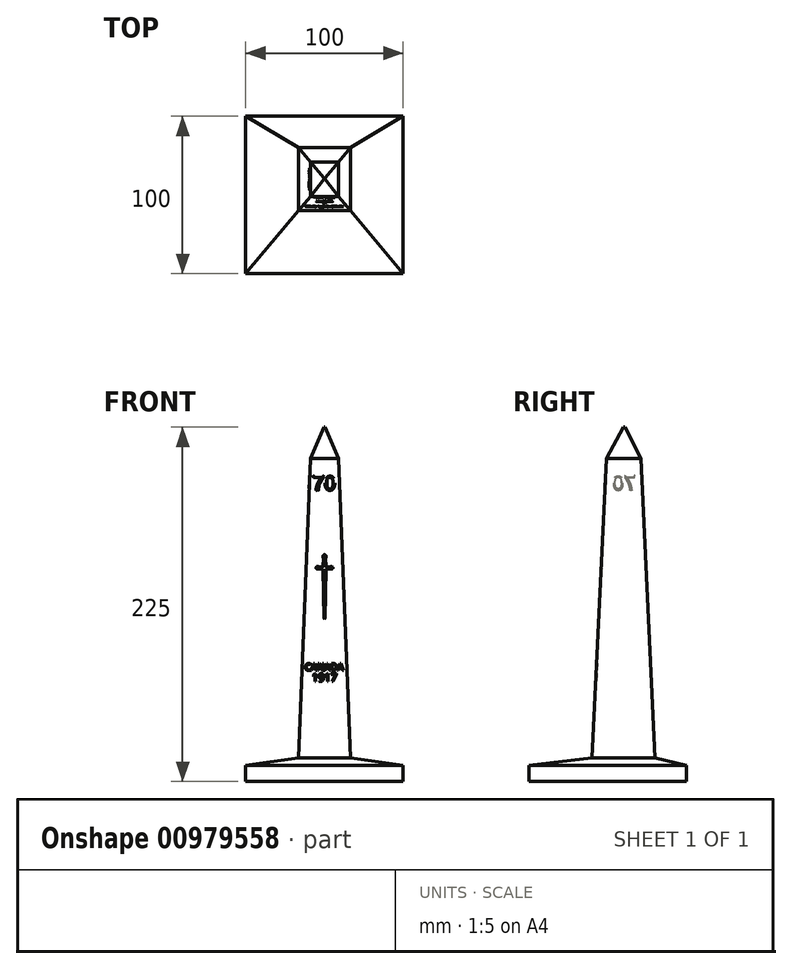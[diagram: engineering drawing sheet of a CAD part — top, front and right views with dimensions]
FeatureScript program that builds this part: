
annotation { "Feature Type Name" : "Feature", "Feature Type Description" : "" }
export const myFeature = defineFeature(function(context is Context, id is Id, definition is map)
    precondition{}
    {
        {
            var Q0;
            Q0=qCreatedBy(makeId("Top.planeOp"),FACE);
            cPlane(context, id + "F0", {"entities" : qUnion([Q0]), "cplaneType" : CPlaneType.OFFSET, "offset" : 15 * mm, "width" : 150 * mm, "height" : 150 * mm});
        }
        {
            var Q0;
            Q0=qCreatedBy(makeId("Top.planeOp"),FACE);
            cPlane(context, id + "F1", {"entities" : qUnion([Q0]), "cplaneType" : CPlaneType.OFFSET, "offset" : 205 * mm, "width" : 150 * mm, "height" : 150 * mm});
        }
        {
            var Q0;
            Q0=qCreatedBy(makeId("Top.planeOp"),FACE);
            cPlane(context, id + "F2", {"entities" : qUnion([Q0]), "cplaneType" : CPlaneType.OFFSET, "offset" : 225 * mm, "width" : 150 * mm, "height" : 150 * mm});
        }
        {
            var Q0;
            Q0=qCreatedBy(makeId("Top.planeOp"),FACE);
            var sketch = newSketch(context, id + "F3", { "sketchPlane" : qUnion([Q0])});
            skLineSegment(sketch, "E0.bottom", {"start": v(-50, 50) * mm, "end": v(50, 50) * mm});
            skLineSegment(sketch, "E0.top", {"start": v(-50, -50) * mm, "end": v(50, -50) * mm});
            skLineSegment(sketch, "E0.left", {"start": v(-50, 50) * mm, "end": v(-50, -50) * mm});
            skLineSegment(sketch, "E0.right", {"start": v(50, 50) * mm, "end": v(50, -50) * mm});
            skPoint(sketch, "E0.middle", {"position": v(0, 0) * mm});
            skSolve(sketch);
        }
        {
            var Q0;
            Q0=makeQuery(id+"F3.imprint","IMPRINT",FACE,{"disambiguationData":[TD([[makeQuery(id+"F3.imprint","IMPRINT",EDGE,{"derivedFrom":sQuery(id+"F3.wireOp",EDGE,"E0.bottom")}),-1.0]])]});
            extrude(context, id + "F4", {"entities" : qUnion([Q0]), "depth" : 10 * mm, "offsetDistance" : 25 * mm});
        }
        {
            var Q0;
            Q0=qCreatedBy(id+"F0.planeOp",FACE);
            var sketch = newSketch(context, id + "F5", { "sketchPlane" : qUnion([Q0])});
            skLineSegment(sketch, "E1.bottom", {"start": v(-16.5, 30) * mm, "end": v(16.5, 30) * mm});
            skLineSegment(sketch, "E1.top", {"start": v(-16.5, -10) * mm, "end": v(16.5, -10) * mm});
            skLineSegment(sketch, "E1.left", {"start": v(-16.5, 30) * mm, "end": v(-16.5, -10) * mm});
            skLineSegment(sketch, "E1.right", {"start": v(16.5, 30) * mm, "end": v(16.5, -10) * mm});
            skPoint(sketch, "E1.middle", {"position": v(0, 0) * mm});
            skSolve(sketch);
        }
        {
            var Q0;
            Q0=qCreatedBy(id+"F1.planeOp",FACE);
            var sketch = newSketch(context, id + "F6", { "sketchPlane" : qUnion([Q0])});
            skLineSegment(sketch, "E2.bottom", {"start": v(-9, 21) * mm, "end": v(9, 21) * mm});
            skLineSegment(sketch, "E2.top", {"start": v(-9, -1) * mm, "end": v(9, -1) * mm});
            skLineSegment(sketch, "E2.left", {"start": v(-9, 21) * mm, "end": v(-9, -1) * mm});
            skLineSegment(sketch, "E2.right", {"start": v(9, 21) * mm, "end": v(9, -1) * mm});
            skCircle(sketch, "E3", {"center": v(0, 10) * mm, "radius": 14.21 * mm, "construction": true});
            skSolve(sketch);
        }
        {
            var Q0;
            Q0=qCreatedBy(id+"F2.planeOp",FACE);
            var sketch = newSketch(context, id + "F7", { "sketchPlane" : qUnion([Q0])});
            skLineSegment(sketch, "E4.bottom", {"start": v(-0.4, 10.8) * mm, "end": v(0.4, 10.8) * mm});
            skLineSegment(sketch, "E4.top", {"start": v(-0.4, 10) * mm, "end": v(0.4, 10) * mm});
            skLineSegment(sketch, "E4.left", {"start": v(-0.4, 10.8) * mm, "end": v(-0.4, 10) * mm});
            skLineSegment(sketch, "E4.right", {"start": v(0.4, 10.8) * mm, "end": v(0.4, 10) * mm});
            skPoint(sketch, "E4.middle", {"position": v(0, 0) * mm});
            skSolve(sketch);
        }
        {
            var Q1;
            Q1=makeQuery(id+"F4.opExtrude","CAP_FACE",FACE,{"disambiguationData":[OSD([sQuery(id+"F3.wireOp",EDGE,"E0.bottom"),sQuery(id+"F3.wireOp",EDGE,"E0.top"),sQuery(id+"F3.wireOp",EDGE,"E0.left"),sQuery(id+"F3.wireOp",EDGE,"E0.right")])],"isStart":false});
            var Q2;
            Q2=makeQuery(id+"F5.imprint","IMPRINT",FACE,{"disambiguationData":[TD([[makeQuery(id+"F5.imprint","IMPRINT",EDGE,{"derivedFrom":sQuery(id+"F5.wireOp",EDGE,"E1.bottom")}),-1.0]])]});
            loft(context, id + "F8", {"operationType" : NewBodyOperationType.ADD, "sheetProfilesArray" : [{ "sheetProfileEntities" : qUnion([Q1]) }, { "sheetProfileEntities" : qUnion([Q2]) }]});
        }
        {
            var Q1;
            Q1=makeQuery(id+"F5.imprint","IMPRINT",FACE,{"disambiguationData":[TD([[makeQuery(id+"F5.imprint","IMPRINT",EDGE,{"derivedFrom":sQuery(id+"F5.wireOp",EDGE,"E1.bottom")}),-1.0]])]});
            var Q2;
            Q2=makeQuery(id+"F6.imprint","IMPRINT",FACE,{"disambiguationData":[TD([[makeQuery(id+"F6.imprint","IMPRINT",EDGE,{"derivedFrom":sQuery(id+"F6.wireOp",EDGE,"E2.bottom")}),-1.0]])]});
            loft(context, id + "F9", {"operationType" : NewBodyOperationType.ADD, "sheetProfilesArray" : [{ "sheetProfileEntities" : qUnion([Q1]) }, { "sheetProfileEntities" : qUnion([Q2]) }]});
        }
        {
            var Q1;
            Q1=makeQuery(id+"F9.opLoft","CAP_FACE",FACE,{"disambiguationData":[OSD([makeQuery(id+"F6.imprint","IMPRINT",FACE,{"disambiguationData":[TD([[makeQuery(id+"F6.imprint","IMPRINT",EDGE,{"derivedFrom":sQuery(id+"F6.wireOp",EDGE,"E2.bottom")}),-1.0]])]})])],"isStart":true});
            var Q2;
            Q2=makeQuery(id+"F7.imprint","IMPRINT",FACE,{"disambiguationData":[TD([[makeQuery(id+"F7.imprint","IMPRINT",EDGE,{"derivedFrom":sQuery(id+"F7.wireOp",EDGE,"E4.bottom")}),-1.0]])]});
            loft(context, id + "F10", {"operationType" : NewBodyOperationType.ADD, "sheetProfilesArray" : [{ "sheetProfileEntities" : qUnion([Q1]) }, { "sheetProfileEntities" : qUnion([Q2]) }]});
        }
        {
            var Q0;
            Q0=makeQuery(id+"F9.opLoft","SWEPT_FACE",FACE,{"disambiguationData":[OSD([sQuery(id+"F5.wireOp",EDGE,"E1.top"),sQuery(id+"F5.wireOp",EDGE,"E1.left"),sQuery(id+"F5.wireOp",EDGE,"E1.right"),sQuery(id+"F6.wireOp",EDGE,"E2.top"),sQuery(id+"F6.wireOp",EDGE,"E2.left"),sQuery(id+"F6.wireOp",EDGE,"E2.right")])]});
            var sketch = newSketch(context, id + "F11", { "sketchPlane" : qUnion([Q0])});
            skText(sketch, "E5", { "text": "70", "fontName": "Arimo-Regular.ttf"});
            const initialGuessF11  = {"E5": [-0.0075, 0.18463, 1, 0, 0.00945]};
            skSetInitialGuess(sketch, initialGuessF11);
            skSolve(sketch);
        }
        {
            var Q0;
            Q0=makeQuery(id+"F9.opLoft","SWEPT_FACE",FACE,{"disambiguationData":[OSD([sQuery(id+"F5.wireOp",EDGE,"E1.bottom"),sQuery(id+"F5.wireOp",EDGE,"E1.top"),sQuery(id+"F5.wireOp",EDGE,"E1.left"),sQuery(id+"F6.wireOp",EDGE,"E2.bottom"),sQuery(id+"F6.wireOp",EDGE,"E2.top"),sQuery(id+"F6.wireOp",EDGE,"E2.left")])]});
            var sketch = newSketch(context, id + "F12", { "sketchPlane" : qUnion([Q0])});
            skText(sketch, "E6", { "text": "70", "fontName": "Arimo-Regular.ttf"});
            skLineSegment(sketch, "E7.0", {"start": v(1.95, 184.5) * mm, "end": v(1.95, 185.09) * mm});
            const initialGuessF12  = {"E6": [-0.0175, 0.1845, 1, 0, 0.00945]};
            skSetInitialGuess(sketch, initialGuessF12);
            skSolve(sketch);
        }
        {
            var Q0;
            {var subQ0=sQuery(id+"F6.wireOp",EDGE,"E2.left");var subQ1=sQuery(id+"F6.wireOp",EDGE,"E2.top");var subQ3=sQuery(id+"F5.wireOp",EDGE,"E1.left");var subQ4=sQuery(id+"F5.wireOp",EDGE,"E1.top");var subQ6=sQuery(id+"F5.wireOp",EDGE,"E1.right");var subQ11=sQuery(id+"F6.wireOp",EDGE,"E2.right");Q0=makeQuery(id+"F14.boolean.opBoolean","SPLIT",FACE,{"disambiguationData":[TD([makeQuery(id+"F14.opExtrude","SWEPT_FACE",FACE,{"disambiguationData":[OSD([sQuery(id+"F11.wireOp",EDGE,"E5.sketch_text.stroke-0")])]})])],"derivedFrom":makeQuery(id+"F9.opLoft","SWEPT_FACE",FACE,{"disambiguationData":[OSD([subQ4,subQ3,subQ6,subQ1,subQ0,subQ11])]})});}
            var sketch = newSketch(context, id + "F13", { "sketchPlane" : qUnion([Q0])});
            skLineSegment(sketch, "E8", {"start": v(0, 102.63) * mm, "end": v(-0.4, 103.13) * mm});
            skLineSegment(sketch, "E9", {"start": v(-0.4, 103.13) * mm, "end": v(-1, 134.43) * mm});
            skLineSegment(sketch, "E10", {"start": v(-1, 134.43) * mm, "end": v(-3.74, 134.68) * mm});
            skLineSegment(sketch, "E11", {"start": v(0, 102.63) * mm, "end": v(0, 143.63) * mm, "construction": true});
            skCircle(sketch, "E12", {"center": v(-4.4, 135.29) * mm, "radius": 0.9 * mm});
            skPoint(sketch, "E12.second.point", {"position": v(-3.74, 135.9) * mm});
            skPoint(sketch, "E12.third.point", {"position": v(-5.3, 135.25) * mm});
            skLineSegment(sketch, "E13", {"start": v(-3.74, 135.9) * mm, "end": v(-1, 136.03) * mm});
            skLineSegment(sketch, "E14", {"start": v(-1, 136.03) * mm, "end": v(-0.66, 141.52) * mm});
            skArc(sketch, "E15", {"start": v(0, 143.63) * mm, "mid": v(-1.03, 142.8) * mm, "end": v(-0.66, 141.52) * mm});
            skArc(sketch, "E16.MirrorCS", {"start": v(0, 143.63) * mm, "mid": v(1.03, 142.8) * mm, "end": v(0.66, 141.52) * mm});
            skLineSegment(sketch, "E17.MirrorCS", {"start": v(1, 136.03) * mm, "end": v(0.66, 141.52) * mm});
            skLineSegment(sketch, "E18.MirrorCS", {"start": v(3.74, 135.9) * mm, "end": v(1, 136.03) * mm});
            skCircle(sketch, "E19.MirrorC", {"center": v(4.4, 135.29) * mm, "radius": 0.9 * mm});
            skLineSegment(sketch, "E20.MirrorCS", {"start": v(1, 134.43) * mm, "end": v(3.74, 134.68) * mm});
            skLineSegment(sketch, "E21.MirrorCS", {"start": v(0.4, 103.13) * mm, "end": v(1, 134.43) * mm});
            skLineSegment(sketch, "E22.MirrorCS", {"start": v(0, 102.63) * mm, "end": v(0.4, 103.13) * mm});
            skSolve(sketch);
        }
        {
            var Q0;
            Q0=qSketchRegion(id+"F11",true);
            extrude(context, id + "F14", {"entities" : qUnion([Q0]), "operationType" : NewBodyOperationType.REMOVE, "oppositeDirection" : true, "depth" : .4 * mm, "offsetDistance" : 25 * mm});
        }
        {
            var Q0;
            Q0 = qSketchRegion(id + "F12", true);
            extrude(context, id + "F15", {"entities" : qUnion([Q0]), "operationType" : NewBodyOperationType.REMOVE, "oppositeDirection" : true, "depth" : .4 * mm, "offsetDistance" : 25 * mm});
        }
        {
            var Q0;
            Q0=qSketchRegion(id+"F13",true);
            extrude(context, id + "F16", {"entities" : qUnion([Q0]), "operationType" : NewBodyOperationType.REMOVE, "oppositeDirection" : true, "depth" : .4 * mm, "offsetDistance" : 25 * mm});
        }
        {
            var Q0;
            Q0=makeQuery(id+"F14.boolean.opBoolean","COPY",EDGE,{"derivedFrom":makeQuery(id+"F14.opExtrude","CAP_EDGE",EDGE,{"disambiguationData":[OSD([sQuery(id+"F11.wireOp",EDGE,"E5.sketch_text.stroke-5")])],"isStart":true})});
            var Q1;
            Q1=makeQuery(id+"F14.boolean.opBoolean","COPY",EDGE,{"derivedFrom":makeQuery(id+"F14.opExtrude","CAP_EDGE",EDGE,{"disambiguationData":[OSD([sQuery(id+"F11.wireOp",EDGE,"E5.sketch_text.stroke-6")])],"isStart":true})});
            var Q2;
            Q2=makeQuery(id+"F14.boolean.opBoolean","COPY",EDGE,{"derivedFrom":makeQuery(id+"F14.opExtrude","CAP_EDGE",EDGE,{"disambiguationData":[OSD([sQuery(id+"F11.wireOp",EDGE,"E5.sketch_text.stroke-7")])],"isStart":true})});
            var Q3;
            Q3=makeQuery(id+"F14.boolean.opBoolean","COPY",EDGE,{"derivedFrom":makeQuery(id+"F14.opExtrude","CAP_EDGE",EDGE,{"disambiguationData":[OSD([sQuery(id+"F11.wireOp",EDGE,"E5.sketch_text.stroke-8")])],"isStart":true})});
            var Q4;
            Q4=makeQuery(id+"F14.boolean.opBoolean","COPY",EDGE,{"derivedFrom":makeQuery(id+"F14.opExtrude","CAP_EDGE",EDGE,{"disambiguationData":[OSD([sQuery(id+"F11.wireOp",EDGE,"E5.sketch_text.stroke-0")])],"isStart":true})});
            var Q5;
            Q5=makeQuery(id+"F14.boolean.opBoolean","COPY",EDGE,{"derivedFrom":makeQuery(id+"F14.opExtrude","CAP_EDGE",EDGE,{"disambiguationData":[OSD([sQuery(id+"F11.wireOp",EDGE,"E5.sketch_text.stroke-9")])],"isStart":true})});
            var Q6;
            Q6=makeQuery(id+"F14.boolean.opBoolean","COPY",EDGE,{"derivedFrom":makeQuery(id+"F14.opExtrude","CAP_EDGE",EDGE,{"disambiguationData":[OSD([sQuery(id+"F11.wireOp",EDGE,"E5.sketch_text.stroke-1")])],"isStart":true})});
            var Q7;
            Q7=makeQuery(id+"F14.boolean.opBoolean","COPY",EDGE,{"derivedFrom":makeQuery(id+"F14.opExtrude","CAP_EDGE",EDGE,{"disambiguationData":[OSD([sQuery(id+"F11.wireOp",EDGE,"E5.sketch_text.stroke-2")])],"isStart":true})});
            var Q8;
            Q8=makeQuery(id+"F14.boolean.opBoolean","COPY",EDGE,{"derivedFrom":makeQuery(id+"F14.opExtrude","CAP_EDGE",EDGE,{"disambiguationData":[OSD([sQuery(id+"F11.wireOp",EDGE,"E5.sketch_text.stroke-3")])],"isStart":true})});
            var Q9;
            Q9=makeQuery(id+"F14.boolean.opBoolean","COPY",EDGE,{"derivedFrom":makeQuery(id+"F14.opExtrude","CAP_EDGE",EDGE,{"disambiguationData":[OSD([sQuery(id+"F11.wireOp",EDGE,"E5.sketch_text.stroke-4")])],"isStart":true})});
            var Q10;
            Q10=makeQuery(id+"F14.boolean.opBoolean","COPY",EDGE,{"derivedFrom":makeQuery(id+"F14.opExtrude","CAP_EDGE",EDGE,{"disambiguationData":[OSD([sQuery(id+"F11.wireOp",EDGE,"E5.sketch_text.stroke-6")])],"isStart":false})});
            var Q11;
            Q11=makeQuery(id+"F14.boolean.opBoolean","COPY",EDGE,{"derivedFrom":makeQuery(id+"F14.opExtrude","CAP_EDGE",EDGE,{"disambiguationData":[OSD([sQuery(id+"F11.wireOp",EDGE,"E5.sketch_text.stroke-7")])],"isStart":false})});
            var Q12;
            Q12=makeQuery(id+"F14.boolean.opBoolean","COPY",EDGE,{"derivedFrom":makeQuery(id+"F14.opExtrude","CAP_EDGE",EDGE,{"disambiguationData":[OSD([sQuery(id+"F11.wireOp",EDGE,"E5.sketch_text.stroke-8")])],"isStart":false})});
            var Q13;
            Q13=makeQuery(id+"F14.boolean.opBoolean","COPY",EDGE,{"derivedFrom":makeQuery(id+"F14.opExtrude","CAP_EDGE",EDGE,{"disambiguationData":[OSD([sQuery(id+"F11.wireOp",EDGE,"E5.sketch_text.stroke-9")])],"isStart":false})});
            var Q14;
            Q14=makeQuery(id+"F14.boolean.opBoolean","COPY",EDGE,{"derivedFrom":makeQuery(id+"F14.opExtrude","CAP_EDGE",EDGE,{"disambiguationData":[OSD([sQuery(id+"F11.wireOp",EDGE,"E5.sketch_text.stroke-0")])],"isStart":false})});
            var Q15;
            Q15=makeQuery(id+"F14.boolean.opBoolean","COPY",EDGE,{"derivedFrom":makeQuery(id+"F14.opExtrude","CAP_EDGE",EDGE,{"disambiguationData":[OSD([sQuery(id+"F11.wireOp",EDGE,"E5.sketch_text.stroke-3")])],"isStart":false})});
            var Q16;
            Q16=makeQuery(id+"F14.boolean.opBoolean","COPY",EDGE,{"derivedFrom":makeQuery(id+"F14.opExtrude","CAP_EDGE",EDGE,{"disambiguationData":[OSD([sQuery(id+"F11.wireOp",EDGE,"E5.sketch_text.stroke-4")])],"isStart":false})});
            var Q17;
            Q17=makeQuery(id+"F14.boolean.opBoolean","COPY",EDGE,{"derivedFrom":makeQuery(id+"F14.opExtrude","CAP_EDGE",EDGE,{"disambiguationData":[OSD([sQuery(id+"F11.wireOp",EDGE,"E5.sketch_text.stroke-5")])],"isStart":false})});
            var Q18;
            Q18=makeQuery(id+"F14.boolean.opBoolean","COPY",EDGE,{"derivedFrom":makeQuery(id+"F14.opExtrude","CAP_EDGE",EDGE,{"disambiguationData":[OSD([sQuery(id+"F11.wireOp",EDGE,"E5.sketch_text.stroke-1")])],"isStart":false})});
            var Q19;
            Q19=makeQuery(id+"F14.boolean.opBoolean","COPY",EDGE,{"derivedFrom":makeQuery(id+"F14.opExtrude","CAP_EDGE",EDGE,{"disambiguationData":[OSD([sQuery(id+"F11.wireOp",EDGE,"E5.sketch_text.stroke-2")])],"isStart":false})});
            var Q20;
            Q20=makeQuery(id+"F14.boolean.opBoolean","COPY",EDGE,{"derivedFrom":makeQuery(id+"F14.opExtrude","CAP_EDGE",EDGE,{"disambiguationData":[OSD([sQuery(id+"F11.wireOp",EDGE,"E5.sketch_text.stroke-10")])],"isStart":false})});
            var Q21;
            Q21=makeQuery(id+"F14.boolean.opBoolean","COPY",EDGE,{"derivedFrom":makeQuery(id+"F14.opExtrude","CAP_EDGE",EDGE,{"disambiguationData":[OSD([sQuery(id+"F11.wireOp",EDGE,"E5.sketch_text.stroke-10")])],"isStart":true})});
            var Q22;
            Q22=makeQuery(id+"F14.boolean.opBoolean","COPY",EDGE,{"derivedFrom":makeQuery(id+"F14.opExtrude","CAP_EDGE",EDGE,{"disambiguationData":[OSD([sQuery(id+"F11.wireOp",EDGE,"E5.sketch_text.stroke-22")])],"isStart":false})});
            var Q23;
            Q23=makeQuery(id+"F14.boolean.opBoolean","COPY",EDGE,{"derivedFrom":makeQuery(id+"F14.opExtrude","CAP_EDGE",EDGE,{"disambiguationData":[OSD([sQuery(id+"F11.wireOp",EDGE,"E5.sketch_text.stroke-21")])],"isStart":true})});
            var Q24;
            Q24=makeQuery(id+"F14.boolean.opBoolean","COPY",EDGE,{"derivedFrom":makeQuery(id+"F14.opExtrude","CAP_EDGE",EDGE,{"disambiguationData":[OSD([sQuery(id+"F13.wireOp",EDGE,"E15")])],"isStart":false})});
            var Q25;
            Q25=makeQuery(id+"F14.boolean.opBoolean","COPY",EDGE,{"derivedFrom":makeQuery(id+"F14.opExtrude","CAP_EDGE",EDGE,{"disambiguationData":[OSD([sQuery(id+"F13.wireOp",EDGE,"E16.MirrorCS")])],"isStart":false})});
            var Q26;
            Q26=makeQuery(id+"F14.boolean.opBoolean","COPY",EDGE,{"derivedFrom":makeQuery(id+"F14.opExtrude","CAP_EDGE",EDGE,{"disambiguationData":[OSD([sQuery(id+"F13.wireOp",EDGE,"E16.MirrorCS")])],"isStart":true})});
            var Q27;
            Q27=makeQuery(id+"F14.boolean.opBoolean","COPY",EDGE,{"derivedFrom":makeQuery(id+"F14.opExtrude","CAP_EDGE",EDGE,{"disambiguationData":[OSD([sQuery(id+"F13.wireOp",EDGE,"E15")])],"isStart":true})});
            var Q28;
            Q28=makeQuery(id+"F14.boolean.opBoolean","COPY",EDGE,{"derivedFrom":makeQuery(id+"F14.opExtrude","CAP_EDGE",EDGE,{"disambiguationData":[OSD([sQuery(id+"F13.wireOp",EDGE,"E17.MirrorCS")])],"isStart":false})});
            var Q29;
            Q29=makeQuery(id+"F14.boolean.opBoolean","COPY",EDGE,{"derivedFrom":makeQuery(id+"F14.opExtrude","CAP_EDGE",EDGE,{"disambiguationData":[OSD([sQuery(id+"F13.wireOp",EDGE,"E17.MirrorCS")])],"isStart":true})});
            var Q30;
            Q30=makeQuery(id+"F14.boolean.opBoolean","COPY",EDGE,{"derivedFrom":makeQuery(id+"F14.opExtrude","CAP_EDGE",EDGE,{"disambiguationData":[OSD([sQuery(id+"F13.wireOp",EDGE,"E14")])],"isStart":false})});
            var Q31;
            Q31=makeQuery(id+"F14.boolean.opBoolean","COPY",EDGE,{"derivedFrom":makeQuery(id+"F14.opExtrude","CAP_EDGE",EDGE,{"disambiguationData":[OSD([sQuery(id+"F13.wireOp",EDGE,"E14")])],"isStart":true})});
            var Q32;
            Q32=makeQuery(id+"F14.boolean.opBoolean","COPY",EDGE,{"derivedFrom":makeQuery(id+"F14.opExtrude","CAP_EDGE",EDGE,{"disambiguationData":[OSD([sQuery(id+"F13.wireOp",EDGE,"E13")])],"isStart":false})});
            var Q33;
            Q33=makeQuery(id+"F14.boolean.opBoolean","COPY",EDGE,{"derivedFrom":makeQuery(id+"F14.opExtrude","CAP_EDGE",EDGE,{"disambiguationData":[OSD([sQuery(id+"F13.wireOp",EDGE,"E13")])],"isStart":true})});
            var Q34;
            Q34=makeQuery(id+"F14.boolean.opBoolean","COPY",EDGE,{"derivedFrom":makeQuery(id+"F14.opExtrude","CAP_EDGE",EDGE,{"disambiguationData":[OSD([sQuery(id+"F13.wireOp",EDGE,"E12")])],"isStart":false})});
            var Q35;
            Q35=makeQuery(id+"F14.boolean.opBoolean","COPY",EDGE,{"derivedFrom":makeQuery(id+"F14.opExtrude","CAP_EDGE",EDGE,{"disambiguationData":[OSD([sQuery(id+"F13.wireOp",EDGE,"E12")])],"isStart":true})});
            var Q36;
            Q36=makeQuery(id+"F14.boolean.opBoolean","COPY",EDGE,{"derivedFrom":makeQuery(id+"F14.opExtrude","CAP_EDGE",EDGE,{"disambiguationData":[OSD([sQuery(id+"F13.wireOp",EDGE,"E18.MirrorCS")])],"isStart":false})});
            var Q37;
            Q37=makeQuery(id+"F14.boolean.opBoolean","COPY",EDGE,{"derivedFrom":makeQuery(id+"F14.opExtrude","CAP_EDGE",EDGE,{"disambiguationData":[OSD([sQuery(id+"F13.wireOp",EDGE,"E18.MirrorCS")])],"isStart":true})});
            var Q38;
            Q38=makeQuery(id+"F14.boolean.opBoolean","COPY",EDGE,{"derivedFrom":makeQuery(id+"F14.opExtrude","CAP_EDGE",EDGE,{"disambiguationData":[OSD([sQuery(id+"F13.wireOp",EDGE,"E19.MirrorC")])],"isStart":false})});
            var Q39;
            Q39=makeQuery(id+"F14.boolean.opBoolean","COPY",EDGE,{"derivedFrom":makeQuery(id+"F14.opExtrude","CAP_EDGE",EDGE,{"disambiguationData":[OSD([sQuery(id+"F13.wireOp",EDGE,"E19.MirrorC")])],"isStart":true})});
            var Q40;
            Q40=makeQuery(id+"F14.boolean.opBoolean","COPY",EDGE,{"derivedFrom":makeQuery(id+"F14.opExtrude","CAP_EDGE",EDGE,{"disambiguationData":[OSD([sQuery(id+"F13.wireOp",EDGE,"E20.MirrorCS")])],"isStart":false})});
            var Q41;
            Q41=makeQuery(id+"F14.boolean.opBoolean","COPY",EDGE,{"derivedFrom":makeQuery(id+"F14.opExtrude","CAP_EDGE",EDGE,{"disambiguationData":[OSD([sQuery(id+"F13.wireOp",EDGE,"E20.MirrorCS")])],"isStart":true})});
            var Q42;
            Q42=makeQuery(id+"F14.boolean.opBoolean","COPY",EDGE,{"derivedFrom":makeQuery(id+"F14.opExtrude","CAP_EDGE",EDGE,{"disambiguationData":[OSD([sQuery(id+"F13.wireOp",EDGE,"E10")])],"isStart":false})});
            var Q43;
            Q43=makeQuery(id+"F14.boolean.opBoolean","COPY",EDGE,{"derivedFrom":makeQuery(id+"F14.opExtrude","CAP_EDGE",EDGE,{"disambiguationData":[OSD([sQuery(id+"F13.wireOp",EDGE,"E21.MirrorCS")])],"isStart":false})});
            var Q44;
            Q44=makeQuery(id+"F14.boolean.opBoolean","COPY",EDGE,{"derivedFrom":makeQuery(id+"F14.opExtrude","CAP_EDGE",EDGE,{"disambiguationData":[OSD([sQuery(id+"F13.wireOp",EDGE,"E21.MirrorCS")])],"isStart":true})});
            var Q45;
            Q45=makeQuery(id+"F14.boolean.opBoolean","COPY",EDGE,{"derivedFrom":makeQuery(id+"F14.opExtrude","CAP_EDGE",EDGE,{"disambiguationData":[OSD([sQuery(id+"F13.wireOp",EDGE,"E10")])],"isStart":true})});
            var Q46;
            Q46=makeQuery(id+"F14.boolean.opBoolean","COPY",EDGE,{"derivedFrom":makeQuery(id+"F14.opExtrude","CAP_EDGE",EDGE,{"disambiguationData":[OSD([sQuery(id+"F13.wireOp",EDGE,"E9")])],"isStart":false})});
            var Q47;
            Q47=makeQuery(id+"F14.boolean.opBoolean","COPY",EDGE,{"derivedFrom":makeQuery(id+"F14.opExtrude","CAP_EDGE",EDGE,{"disambiguationData":[OSD([sQuery(id+"F13.wireOp",EDGE,"E9")])],"isStart":true})});
            var Q48;
            Q48=makeQuery(id+"F14.boolean.opBoolean","COPY",EDGE,{"derivedFrom":makeQuery(id+"F14.opExtrude","CAP_EDGE",EDGE,{"disambiguationData":[OSD([sQuery(id+"F13.wireOp",EDGE,"E22.MirrorCS")])],"isStart":false})});
            var Q49;
            Q49=makeQuery(id+"F14.boolean.opBoolean","COPY",EDGE,{"derivedFrom":makeQuery(id+"F14.opExtrude","CAP_EDGE",EDGE,{"disambiguationData":[OSD([sQuery(id+"F13.wireOp",EDGE,"E22.MirrorCS")])],"isStart":true})});
            var Q50;
            Q50=makeQuery(id+"F14.boolean.opBoolean","COPY",EDGE,{"derivedFrom":makeQuery(id+"F14.opExtrude","CAP_EDGE",EDGE,{"disambiguationData":[OSD([sQuery(id+"F13.wireOp",EDGE,"E8")])],"isStart":true})});
            var Q51;
            Q51=makeQuery(id+"F14.boolean.opBoolean","COPY",EDGE,{"derivedFrom":makeQuery(id+"F14.opExtrude","CAP_EDGE",EDGE,{"disambiguationData":[OSD([sQuery(id+"F13.wireOp",EDGE,"E8")])],"isStart":false})});
            var Q52;
            Q52=makeQuery(id+"F15.boolean.opBoolean","COPY",EDGE,{"derivedFrom":makeQuery(id+"F15.opExtrude","CAP_EDGE",EDGE,{"disambiguationData":[OSD([sQuery(id+"F12.wireOp",EDGE,"E6.sketch_text.stroke-8")])],"isStart":true})});
            var Q53;
            Q53=makeQuery(id+"F15.boolean.opBoolean","COPY",EDGE,{"derivedFrom":makeQuery(id+"F15.opExtrude","CAP_EDGE",EDGE,{"disambiguationData":[OSD([sQuery(id+"F12.wireOp",EDGE,"E6.sketch_text.stroke-14")])],"isStart":false})});
            var Q54;
            Q54=makeQuery(id+"F15.boolean.opBoolean","COPY",EDGE,{"derivedFrom":makeQuery(id+"F15.opExtrude","CAP_EDGE",EDGE,{"disambiguationData":[OSD([sQuery(id+"F12.wireOp",EDGE,"E6.sketch_text.stroke-20")])],"isStart":true})});
            var Q55;
            Q55=makeQuery(id+"F15.boolean.opBoolean","COPY",EDGE,{"derivedFrom":makeQuery(id+"F15.opExtrude","CAP_EDGE",EDGE,{"disambiguationData":[OSD([sQuery(id+"F12.wireOp",EDGE,"E6.sketch_text.stroke-5")])],"isStart":true})});
            var Q56;
            Q56=makeQuery(id+"F15.boolean.opBoolean","COPY",EDGE,{"derivedFrom":makeQuery(id+"F15.opExtrude","CAP_EDGE",EDGE,{"disambiguationData":[OSD([sQuery(id+"F12.wireOp",EDGE,"E6.sketch_text.stroke-6")])],"isStart":true})});
            var Q57;
            Q57=makeQuery(id+"F15.boolean.opBoolean","COPY",EDGE,{"derivedFrom":makeQuery(id+"F15.opExtrude","CAP_EDGE",EDGE,{"disambiguationData":[OSD([sQuery(id+"F12.wireOp",EDGE,"E6.sketch_text.stroke-7")])],"isStart":true})});
            var Q58;
            Q58=makeQuery(id+"F15.boolean.opBoolean","COPY",EDGE,{"derivedFrom":makeQuery(id+"F15.opExtrude","CAP_EDGE",EDGE,{"disambiguationData":[OSD([sQuery(id+"F12.wireOp",EDGE,"E6.sketch_text.stroke-0")])],"isStart":true})});
            var Q59;
            Q59=makeQuery(id+"F15.boolean.opBoolean","COPY",EDGE,{"derivedFrom":makeQuery(id+"F15.opExtrude","CAP_EDGE",EDGE,{"disambiguationData":[OSD([sQuery(id+"F12.wireOp",EDGE,"E6.sketch_text.stroke-9")])],"isStart":true})});
            var Q60;
            Q60=makeQuery(id+"F15.boolean.opBoolean","COPY",EDGE,{"derivedFrom":makeQuery(id+"F15.opExtrude","CAP_EDGE",EDGE,{"disambiguationData":[OSD([sQuery(id+"F12.wireOp",EDGE,"E6.sketch_text.stroke-3")])],"isStart":false})});
            var Q61;
            Q61=makeQuery(id+"F15.boolean.opBoolean","COPY",EDGE,{"derivedFrom":makeQuery(id+"F15.opExtrude","CAP_EDGE",EDGE,{"disambiguationData":[OSD([sQuery(id+"F12.wireOp",EDGE,"E6.sketch_text.stroke-14")])],"isStart":true})});
            var Q62;
            Q62=makeQuery(id+"F15.boolean.opBoolean","COPY",EDGE,{"derivedFrom":makeQuery(id+"F15.opExtrude","CAP_EDGE",EDGE,{"disambiguationData":[OSD([sQuery(id+"F12.wireOp",EDGE,"E6.sketch_text.stroke-21")])],"isStart":false})});
            var Q63;
            Q63=makeQuery(id+"F15.boolean.opBoolean","COPY",EDGE,{"derivedFrom":makeQuery(id+"F15.opExtrude","CAP_EDGE",EDGE,{"disambiguationData":[OSD([sQuery(id+"F12.wireOp",EDGE,"E6.sketch_text.stroke-8")])],"isStart":false})});
            var Q64;
            Q64=makeQuery(id+"F15.boolean.opBoolean","COPY",EDGE,{"derivedFrom":makeQuery(id+"F15.opExtrude","CAP_EDGE",EDGE,{"disambiguationData":[OSD([sQuery(id+"F12.wireOp",EDGE,"E6.sketch_text.stroke-7")])],"isStart":false})});
            var Q65;
            Q65=makeQuery(id+"F15.boolean.opBoolean","COPY",EDGE,{"derivedFrom":makeQuery(id+"F15.opExtrude","CAP_EDGE",EDGE,{"disambiguationData":[OSD([sQuery(id+"F12.wireOp",EDGE,"E6.sketch_text.stroke-6")])],"isStart":false})});
            var Q66;
            Q66=makeQuery(id+"F15.boolean.opBoolean","COPY",EDGE,{"derivedFrom":makeQuery(id+"F15.opExtrude","CAP_EDGE",EDGE,{"disambiguationData":[OSD([sQuery(id+"F12.wireOp",EDGE,"E6.sketch_text.stroke-9")])],"isStart":false})});
            var Q67;
            Q67=makeQuery(id+"F15.boolean.opBoolean","COPY",EDGE,{"derivedFrom":makeQuery(id+"F15.opExtrude","CAP_EDGE",EDGE,{"disambiguationData":[OSD([sQuery(id+"F12.wireOp",EDGE,"E6.sketch_text.stroke-0")])],"isStart":false})});
            var Q68;
            Q68=makeQuery(id+"F15.boolean.opBoolean","COPY",EDGE,{"derivedFrom":makeQuery(id+"F15.opExtrude","CAP_EDGE",EDGE,{"disambiguationData":[OSD([sQuery(id+"F12.wireOp",EDGE,"E6.sketch_text.stroke-5")])],"isStart":false})});
            var Q69;
            Q69=makeQuery(id+"F15.boolean.opBoolean","COPY",EDGE,{"derivedFrom":makeQuery(id+"F15.opExtrude","CAP_EDGE",EDGE,{"disambiguationData":[OSD([sQuery(id+"F12.wireOp",EDGE,"E6.sketch_text.stroke-3")])],"isStart":true})});
            fillet(context, id + "F17", {"entities" : qUnion([Q0, Q1, Q2, Q3, Q4, Q5, Q6, Q7, Q8, Q9, Q10, Q11, Q12, Q13, Q14, Q15, Q16, Q17, Q18, Q19, Q20, Q21, Q22, Q23, Q24, Q25, Q26, Q27, Q28, Q29, Q30, Q31, Q32, Q33, Q34, Q35, Q36, Q37, Q38, Q39, Q40, Q41, Q42, Q43, Q44, Q45, Q46, Q47, Q48, Q49, Q50, Q51, Q52, Q53, Q54, Q55, Q56, Q57, Q58, Q59, Q60, Q61, Q62, Q63, Q64, Q65, Q66, Q67, Q68, Q69]), "radius" : .2 * mm, "tangentPropagation" : true, "allowEdgeOverflow" : false});
        }
        {
            var Q0;
            Q0=makeQuery(id+"F16.boolean.opBoolean","COPY",EDGE,{"derivedFrom":makeQuery(id+"F16.opExtrude","CAP_EDGE",EDGE,{"disambiguationData":[OSD([sQuery(id+"F13.wireOp",EDGE,"E16.MirrorCS")])],"isStart":false})});
            var Q1;
            Q1=makeQuery(id+"F16.boolean.opBoolean","COPY",EDGE,{"derivedFrom":makeQuery(id+"F16.opExtrude","CAP_EDGE",EDGE,{"disambiguationData":[OSD([sQuery(id+"F13.wireOp",EDGE,"E16.MirrorCS")])],"isStart":true})});
            var Q2;
            Q2=makeQuery(id+"F16.boolean.opBoolean","COPY",EDGE,{"derivedFrom":makeQuery(id+"F16.opExtrude","CAP_EDGE",EDGE,{"disambiguationData":[OSD([sQuery(id+"F13.wireOp",EDGE,"E15")])],"isStart":true})});
            var Q3;
            Q3=makeQuery(id+"F16.boolean.opBoolean","COPY",EDGE,{"derivedFrom":makeQuery(id+"F16.opExtrude","CAP_EDGE",EDGE,{"disambiguationData":[OSD([sQuery(id+"F13.wireOp",EDGE,"E15")])],"isStart":false})});
            var Q4;
            Q4=makeQuery(id+"F16.boolean.opBoolean","COPY",EDGE,{"derivedFrom":makeQuery(id+"F16.opExtrude","CAP_EDGE",EDGE,{"disambiguationData":[OSD([sQuery(id+"F13.wireOp",EDGE,"E14")])],"isStart":false})});
            var Q5;
            Q5=makeQuery(id+"F16.boolean.opBoolean","COPY",EDGE,{"derivedFrom":makeQuery(id+"F16.opExtrude","CAP_EDGE",EDGE,{"disambiguationData":[OSD([sQuery(id+"F13.wireOp",EDGE,"E14")])],"isStart":true})});
            var Q6;
            Q6=makeQuery(id+"F16.boolean.opBoolean","COPY",EDGE,{"derivedFrom":makeQuery(id+"F16.opExtrude","CAP_EDGE",EDGE,{"disambiguationData":[OSD([sQuery(id+"F13.wireOp",EDGE,"E17.MirrorCS")])],"isStart":false})});
            var Q7;
            Q7=makeQuery(id+"F16.boolean.opBoolean","COPY",EDGE,{"derivedFrom":makeQuery(id+"F16.opExtrude","CAP_EDGE",EDGE,{"disambiguationData":[OSD([sQuery(id+"F13.wireOp",EDGE,"E17.MirrorCS")])],"isStart":true})});
            var Q8;
            Q8=makeQuery(id+"F16.boolean.opBoolean","COPY",EDGE,{"derivedFrom":makeQuery(id+"F16.opExtrude","CAP_EDGE",EDGE,{"disambiguationData":[OSD([sQuery(id+"F13.wireOp",EDGE,"E18.MirrorCS")])],"isStart":false})});
            var Q9;
            Q9=makeQuery(id+"F16.boolean.opBoolean","COPY",EDGE,{"derivedFrom":makeQuery(id+"F16.opExtrude","CAP_EDGE",EDGE,{"disambiguationData":[OSD([sQuery(id+"F13.wireOp",EDGE,"E18.MirrorCS")])],"isStart":true})});
            var Q10;
            Q10=makeQuery(id+"F16.boolean.opBoolean","COPY",EDGE,{"derivedFrom":makeQuery(id+"F16.opExtrude","CAP_EDGE",EDGE,{"disambiguationData":[OSD([sQuery(id+"F13.wireOp",EDGE,"E19.MirrorC")])],"isStart":false})});
            var Q11;
            Q11=makeQuery(id+"F16.boolean.opBoolean","COPY",EDGE,{"derivedFrom":makeQuery(id+"F16.opExtrude","CAP_EDGE",EDGE,{"disambiguationData":[OSD([sQuery(id+"F13.wireOp",EDGE,"E19.MirrorC")])],"isStart":true})});
            var Q12;
            Q12=makeQuery(id+"F16.boolean.opBoolean","COPY",EDGE,{"derivedFrom":makeQuery(id+"F16.opExtrude","CAP_EDGE",EDGE,{"disambiguationData":[OSD([sQuery(id+"F13.wireOp",EDGE,"E20.MirrorCS")])],"isStart":true})});
            var Q13;
            Q13=makeQuery(id+"F16.boolean.opBoolean","COPY",EDGE,{"derivedFrom":makeQuery(id+"F16.opExtrude","CAP_EDGE",EDGE,{"disambiguationData":[OSD([sQuery(id+"F13.wireOp",EDGE,"E20.MirrorCS")])],"isStart":false})});
            var Q14;
            Q14=makeQuery(id+"F16.boolean.opBoolean","COPY",EDGE,{"derivedFrom":makeQuery(id+"F16.opExtrude","CAP_EDGE",EDGE,{"disambiguationData":[OSD([sQuery(id+"F13.wireOp",EDGE,"E10")])],"isStart":true})});
            var Q15;
            Q15=makeQuery(id+"F16.boolean.opBoolean","COPY",EDGE,{"derivedFrom":makeQuery(id+"F16.opExtrude","CAP_EDGE",EDGE,{"disambiguationData":[OSD([sQuery(id+"F13.wireOp",EDGE,"E10")])],"isStart":false})});
            var Q16;
            Q16=makeQuery(id+"F16.boolean.opBoolean","COPY",EDGE,{"derivedFrom":makeQuery(id+"F16.opExtrude","CAP_EDGE",EDGE,{"disambiguationData":[OSD([sQuery(id+"F13.wireOp",EDGE,"E12")])],"isStart":false})});
            var Q17;
            Q17=makeQuery(id+"F16.boolean.opBoolean","COPY",EDGE,{"derivedFrom":makeQuery(id+"F16.opExtrude","CAP_EDGE",EDGE,{"disambiguationData":[OSD([sQuery(id+"F13.wireOp",EDGE,"E12")])],"isStart":true})});
            var Q18;
            Q18=makeQuery(id+"F16.boolean.opBoolean","COPY",EDGE,{"derivedFrom":makeQuery(id+"F16.opExtrude","CAP_EDGE",EDGE,{"disambiguationData":[OSD([sQuery(id+"F13.wireOp",EDGE,"E13")])],"isStart":false})});
            var Q19;
            Q19=makeQuery(id+"F16.boolean.opBoolean","COPY",EDGE,{"derivedFrom":makeQuery(id+"F16.opExtrude","CAP_EDGE",EDGE,{"disambiguationData":[OSD([sQuery(id+"F13.wireOp",EDGE,"E13")])],"isStart":true})});
            var Q20;
            Q20=makeQuery(id+"F16.boolean.opBoolean","COPY",EDGE,{"derivedFrom":makeQuery(id+"F16.opExtrude","CAP_EDGE",EDGE,{"disambiguationData":[OSD([sQuery(id+"F13.wireOp",EDGE,"E21.MirrorCS")])],"isStart":false})});
            var Q21;
            Q21=makeQuery(id+"F16.boolean.opBoolean","COPY",EDGE,{"derivedFrom":makeQuery(id+"F16.opExtrude","CAP_EDGE",EDGE,{"disambiguationData":[OSD([sQuery(id+"F13.wireOp",EDGE,"E21.MirrorCS")])],"isStart":true})});
            var Q22;
            Q22=makeQuery(id+"F16.boolean.opBoolean","COPY",EDGE,{"derivedFrom":makeQuery(id+"F16.opExtrude","CAP_EDGE",EDGE,{"disambiguationData":[OSD([sQuery(id+"F13.wireOp",EDGE,"E9")])],"isStart":false})});
            var Q23;
            Q23=makeQuery(id+"F16.boolean.opBoolean","COPY",EDGE,{"derivedFrom":makeQuery(id+"F16.opExtrude","CAP_EDGE",EDGE,{"disambiguationData":[OSD([sQuery(id+"F13.wireOp",EDGE,"E9")])],"isStart":true})});
            var Q24;
            Q24=makeQuery(id+"F16.boolean.opBoolean","COPY",EDGE,{"derivedFrom":makeQuery(id+"F16.opExtrude","CAP_EDGE",EDGE,{"disambiguationData":[OSD([sQuery(id+"F13.wireOp",EDGE,"E8")])],"isStart":true})});
            var Q25;
            Q25=makeQuery(id+"F16.boolean.opBoolean","COPY",EDGE,{"derivedFrom":makeQuery(id+"F16.opExtrude","CAP_EDGE",EDGE,{"disambiguationData":[OSD([sQuery(id+"F13.wireOp",EDGE,"E8")])],"isStart":false})});
            var Q26;
            Q26=makeQuery(id+"F16.boolean.opBoolean","COPY",EDGE,{"derivedFrom":makeQuery(id+"F16.opExtrude","CAP_EDGE",EDGE,{"disambiguationData":[OSD([sQuery(id+"F13.wireOp",EDGE,"E22.MirrorCS")])],"isStart":false})});
            var Q27;
            Q27=makeQuery(id+"F16.boolean.opBoolean","COPY",EDGE,{"derivedFrom":makeQuery(id+"F16.opExtrude","CAP_EDGE",EDGE,{"disambiguationData":[OSD([sQuery(id+"F13.wireOp",EDGE,"E22.MirrorCS")])],"isStart":true})});
            fillet(context, id + "F18", {"entities" : qUnion([Q0, Q1, Q2, Q3, Q4, Q5, Q6, Q7, Q8, Q9, Q10, Q11, Q12, Q13, Q14, Q15, Q16, Q17, Q18, Q19, Q20, Q21, Q22, Q23, Q24, Q25, Q26, Q27]), "radius" : .2 * mm, "tangentPropagation" : true, "allowEdgeOverflow" : false});
        }
        {
            var Q0;
            {var subQ3=sQuery(id+"F6.wireOp",EDGE,"E2.right");var subQ4=sQuery(id+"F6.wireOp",EDGE,"E2.left");var subQ5=sQuery(id+"F6.wireOp",EDGE,"E2.top");var subQ8=sQuery(id+"F5.wireOp",EDGE,"E1.left");var subQ9=sQuery(id+"F5.wireOp",EDGE,"E1.top");var subQ11=sQuery(id+"F5.wireOp",EDGE,"E1.right");Q0=makeQuery(id+"F14.boolean.opBoolean","SPLIT",FACE,{"disambiguationData":[TD([makeQuery(id+"F14.opExtrude","SWEPT_FACE",FACE,{"disambiguationData":[OSD([sQuery(id+"F11.wireOp",EDGE,"E5.sketch_text.stroke-0")])]})])],"derivedFrom":makeQuery(id+"F9.opLoft","SWEPT_FACE",FACE,{"disambiguationData":[OSD([subQ9,subQ8,subQ11,subQ5,subQ4,subQ3])]})});}
            var sketch = newSketch(context, id + "F19", { "sketchPlane" : qUnion([Q0])});
            skText(sketch, "E23", { "text": "CANADA", "fontName": "OpenSans-Regular.ttf"});
            skText(sketch, "E24", { "text": "1917\n", "fontName": "OpenSans-Regular.ttf"});
            const initialGuessF19  = {"E23": [-0.0125, 0.07, 1, 0, 0.00441], "E24": [-0.00799, 0.063, 1, 0, 0.005]};
            skSetInitialGuess(sketch, initialGuessF19);
            skSolve(sketch);
        }
        {
            var Q0;
            Q0 = qSketchRegion(id + "F19", true);
            extrude(context, id + "F20", {"entities" : qUnion([Q0]), "operationType" : NewBodyOperationType.REMOVE, "oppositeDirection" : true, "depth" : .4 * mm, "offsetDistance" : 25 * mm});
        }
    });
